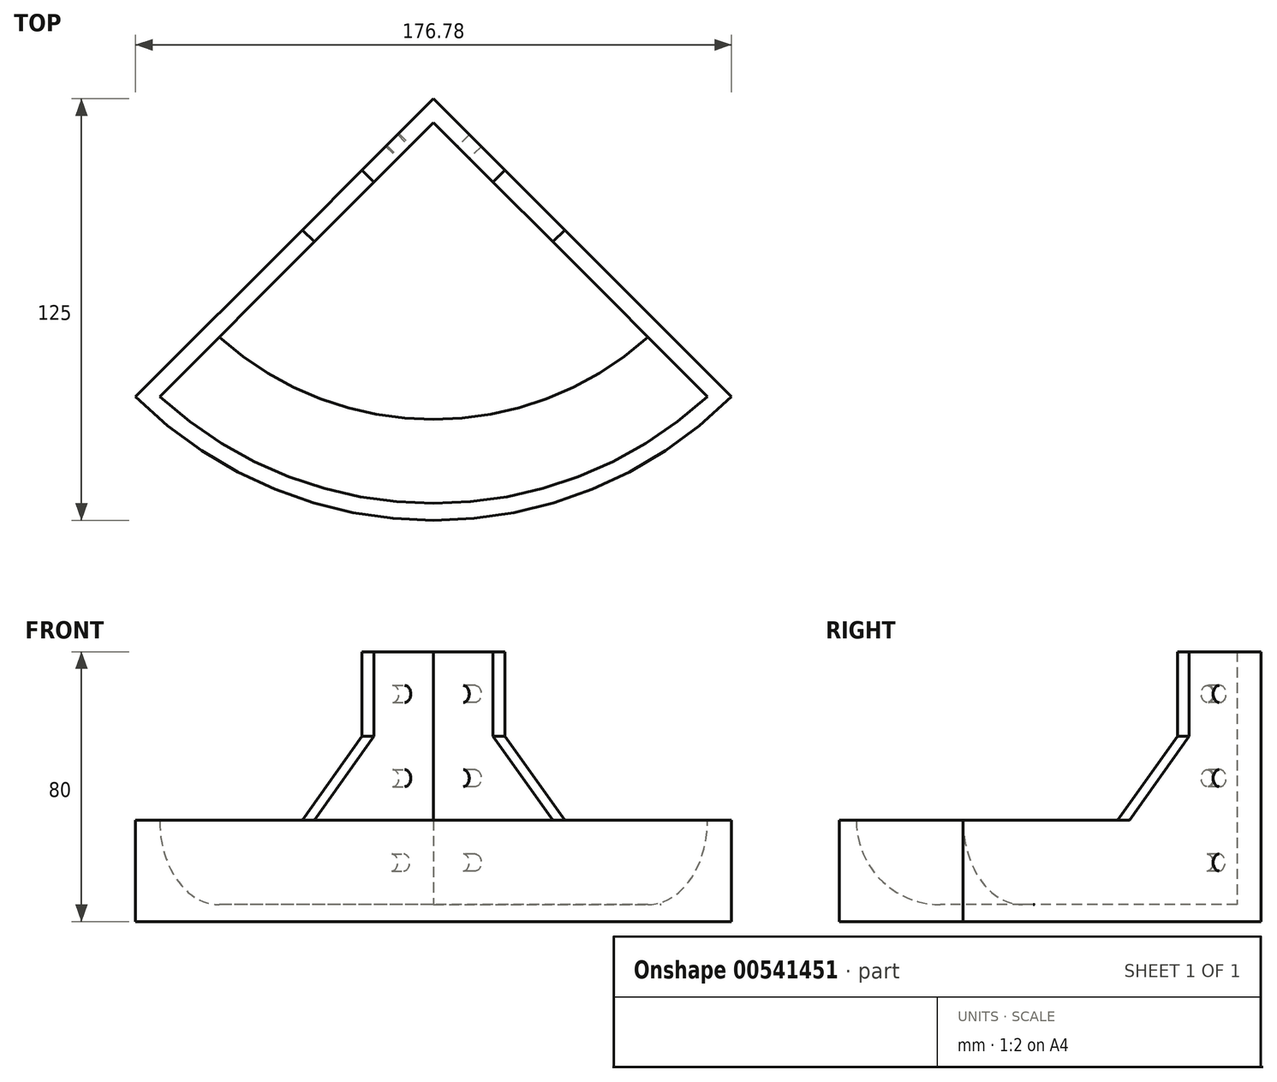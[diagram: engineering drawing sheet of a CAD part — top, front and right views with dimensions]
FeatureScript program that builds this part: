
annotation { "Feature Type Name" : "Feature", "Feature Type Description" : "" }
export const myFeature = defineFeature(function(context is Context, id is Id, definition is map)
    precondition{}
    {
        {
            var Q0;
            Q0=qCreatedBy(makeId("Top.planeOp"),FACE);
            var sketch = newSketch(context, id + "F0", { "sketchPlane" : qUnion([Q0])});
            skLineSegment(sketch, "E0", {"start": v(0, 0) * mm, "end": v(125, 0) * mm});
            skLineSegment(sketch, "E1", {"start": v(0, 0) * mm, "end": v(0, -125) * mm});
            skArc(sketch, "E2", {"start": v(0, -125) * mm, "mid": v(88.39, -88.39) * mm, "end": v(125, 0) * mm});
            skPoint(sketch, "E3", {"position": v(0, -120) * mm});
            skPoint(sketch, "E4", {"position": v(120, 0) * mm});
            skPoint(sketch, "E5", {"position": v(84.85, -84.85) * mm});
            skArc(sketch, "E6", {"start": v(0, -120) * mm, "mid": v(84.85, -84.85) * mm, "end": v(120, 0) * mm});
            skPoint(sketch, "E7", {"position": v(0, -5) * mm});
            skPoint(sketch, "E8", {"position": v(5, 0) * mm});
            skPoint(sketch, "E9", {"position": v(5, -5) * mm});
            skLineSegment(sketch, "E10", {"start": v(5, -5) * mm, "end": v(5, -119.9) * mm});
            skLineSegment(sketch, "E11", {"start": v(5, -5) * mm, "end": v(119.9, -5) * mm});
            skSolve(sketch);
        }
        {
            var Q0;
            {var subQ7=sQuery(id+"F0.wireOp",EDGE,"E10");Q0=makeQuery(id+"F0.imprint","IMPRINT",FACE,{"disambiguationData":[TD([[makeQuery(id+"F0.imprint","IMPRINT",EDGE,{"derivedFrom":subQ7}),-1.0]])]});}
            var Q1;
            {var subQ4=sQuery(id+"F0.wireOp",EDGE,"E2");Q1=makeQuery(id+"F0.imprint","IMPRINT",FACE,{"disambiguationData":[TD([[makeQuery(id+"F0.imprint","IMPRINT",EDGE,{"derivedFrom":subQ4}),1.0]])]});}
            var Q2;
            {var subQ0=sQuery(id+"F0.wireOp",EDGE,"E10");Q2=makeQuery(id+"F0.imprint","IMPRINT",FACE,{"disambiguationData":[TD([[makeQuery(id+"F0.imprint","IMPRINT",EDGE,{"derivedFrom":subQ0}),1.0]])]});}
            extrude(context, id + "F1", {"entities" : qUnion([Q0, Q1, Q2]), "depth" : 5 * mm, "offsetDistance" : 25 * mm});
        }
        {
            var Q0;
            Q0=makeQuery(id+"F1.opExtrude","CAP_FACE",FACE,{"disambiguationData":[OSD([sQuery(id+"F0.wireOp",EDGE,"E0"),sQuery(id+"F0.wireOp",EDGE,"E1"),sQuery(id+"F0.wireOp",EDGE,"E2")])],"isStart":false});
            var sketch = newSketch(context, id + "F2", { "sketchPlane" : qUnion([Q0])});
            skPoint(sketch, "E12", {"position": v(0, -120) * mm});
            skPoint(sketch, "E13", {"position": v(120, 0) * mm});
            skArc(sketch, "E14", {"start": v(0, -120) * mm, "mid": v(84.85, -84.85) * mm, "end": v(120, 0) * mm});
            skPoint(sketch, "E15", {"position": v(0, -5) * mm});
            skPoint(sketch, "E16", {"position": v(5, 0) * mm});
            skLineSegment(sketch, "E17", {"start": v(0, -5) * mm, "end": v(119.9, -5) * mm});
            skLineSegment(sketch, "E18", {"start": v(5, 0) * mm, "end": v(5, -119.9) * mm});
            skSolve(sketch);
        }
        {
            var Q0;
            {var subQ0=sQuery(id+"F2.wireOp",EDGE,"E17");var subQ1=makeQuery(id+"F1.opExtrude","CAP_EDGE",EDGE,{"disambiguationData":[OSD([sQuery(id+"F0.wireOp",EDGE,"E1")])],"isStart":false});var subQ2=makeQuery(id+"F2.imprint","INTERSECT",VERTEX,{"derivedFrom":[subQ1,subQ0]});Q0=makeQuery(id+"F2.imprint","IMPRINT",FACE,{"disambiguationData":[TD([[makeQuery(id+"F2.imprint","IMPRINT",EDGE,{"disambiguationData":[TD([[subQ2,-1.0]])],"derivedFrom":subQ0}),1.0]])]});}
            var Q1;
            {var subQ0=sQuery(id+"F2.wireOp",EDGE,"E14");var subQ1=makeQuery(id+"F1.opExtrude","CAP_EDGE",EDGE,{"disambiguationData":[OSD([sQuery(id+"F0.wireOp",EDGE,"E0")])],"isStart":false});var subQ2=makeQuery(id+"F2.imprint","INTERSECT",VERTEX,{"derivedFrom":[subQ1,subQ0]});Q1=makeQuery(id+"F2.imprint","IMPRINT",FACE,{"disambiguationData":[TD([[makeQuery(id+"F2.imprint","IMPRINT",EDGE,{"disambiguationData":[TD([[subQ2,1.0]])],"derivedFrom":subQ0}),1.0]])]});}
            var Q2;
            {var subQ0=sQuery(id+"F2.wireOp",EDGE,"E14");var subQ1=makeQuery(id+"F1.opExtrude","CAP_EDGE",EDGE,{"disambiguationData":[OSD([sQuery(id+"F0.wireOp",EDGE,"E1")])],"isStart":false});var subQ2=makeQuery(id+"F2.imprint","INTERSECT",VERTEX,{"derivedFrom":[subQ1,subQ0]});Q2=makeQuery(id+"F2.imprint","IMPRINT",FACE,{"disambiguationData":[TD([[makeQuery(id+"F2.imprint","IMPRINT",EDGE,{"disambiguationData":[TD([[subQ2,-1.0]])],"derivedFrom":subQ0}),1.0]])]});}
            var Q3;
            {var subQ0=makeQuery(id+"F1.opExtrude","CAP_EDGE",EDGE,{"disambiguationData":[OSD([sQuery(id+"F0.wireOp",EDGE,"E2")])],"isStart":false});Q3=makeQuery(id+"F2.imprint","IMPRINT",FACE,{"disambiguationData":[TD([[makeQuery(id+"F2.imprint","IMPRINT",EDGE,{"derivedFrom":subQ0}),1.0]])]});}
            extrude(context, id + "F3", {"entities" : qUnion([Q0, Q1, Q2, Q3]), "operationType" : NewBodyOperationType.ADD, "depth" : 25 * mm, "offsetDistance" : 25 * mm});
        }
        {
            var Q0;
            Q0=makeQuery(id+"F3.opExtrude","CAP_FACE",FACE,{"disambiguationData":[OSD([sQuery(id+"F0.wireOp",EDGE,"E0"),sQuery(id+"F0.wireOp",EDGE,"E1"),sQuery(id+"F0.wireOp",EDGE,"E2"),sQuery(id+"F2.wireOp",EDGE,"E14"),sQuery(id+"F2.wireOp",EDGE,"E17"),sQuery(id+"F2.wireOp",EDGE,"E18")])],"isStart":false});
            var sketch = newSketch(context, id + "F4", { "sketchPlane" : qUnion([Q0])});
            skPoint(sketch, "E19", {"position": v(5, -30) * mm});
            skLineSegment(sketch, "E20", {"start": v(5, -30) * mm, "end": v(0, -30) * mm});
            skPoint(sketch, "E21", {"position": v(30, -5) * mm});
            skLineSegment(sketch, "E22", {"start": v(30, -5) * mm, "end": v(30, 0) * mm});
            skSolve(sketch);
        }
        {
            var Q0;
            {var subQ3=sQuery(id+"F4.wireOp",EDGE,"E20");Q0=makeQuery(id+"F4.imprint","IMPRINT",FACE,{"disambiguationData":[TD([[makeQuery(id+"F4.imprint","IMPRINT",EDGE,{"derivedFrom":subQ3}),-1.0]])]});}
            extrude(context, id + "F5", {"entities" : qUnion([Q0]), "operationType" : NewBodyOperationType.ADD, "depth" : 50 * mm, "offsetDistance" : 25 * mm});
        }
        {
            var Q0;
            {var subQ0=sQuery(id+"F2.wireOp",EDGE,"E18");Q0=makeQuery(id+"F5.boolean.opBoolean","MERGE",FACE,{"derivedFrom":[makeQuery(id+"F3.opExtrude","SWEPT_FACE",FACE,{"disambiguationData":[OSD([subQ0])]}),makeQuery(id+"F5.opExtrude","SWEPT_FACE",FACE,{"disambiguationData":[OSD([subQ0])]})]});}
            var sketch = newSketch(context, id + "F6", { "sketchPlane" : qUnion([Q0])});
            skPoint(sketch, "E23", {"position": v(-17.03, 42.5) * mm});
            skPoint(sketch, "E24", {"position": v(-17.03, 67.5) * mm});
            skLineSegment(sketch, "E25", {"start": v(-30, 30) * mm, "end": v(-17.5, 30) * mm});
            skLineSegment(sketch, "E26", {"start": v(-17.5, 30) * mm, "end": v(-17.5, 17.5) * mm});
            skSolve(sketch);
        }
        {
            var Q0;
            Q0=sQuery(id+"F6.wireOp",VERTEX,"E26.end");
            var Q1;
            Q1=sQuery(id+"F6.wireOp",VERTEX,"E23");
            var Q2;
            Q2=sQuery(id+"F6.wireOp",VERTEX,"E24");
            var Q3;
            Q3=makeQuery(id+"F1.opExtrude","SWEPT_BODY",BODY,{"disambiguationData":[OSD([sQuery(id+"F0.wireOp",EDGE,"E0"),sQuery(id+"F0.wireOp",EDGE,"E1"),sQuery(id+"F0.wireOp",EDGE,"E2")])]});
            hole(context, id + "F7", {"style" : HoleStyle.SIMPLE, "endStyle" : HoleEndStyle.BLIND, "holeDiameter" : 5 * mm, "holeDepth" : 10 * mm, "isTappedThrough" : true, "tappedDepth" : 1 * mm, "tapClearance" : 3, "locations" : qUnion([Q0, Q1, Q2]), "scope" : qUnion([Q3])});
        }
        {
            var Q0;
            {var subQ0=sQuery(id+"F2.wireOp",EDGE,"E17");Q0=makeQuery(id+"F5.boolean.opBoolean","MERGE",FACE,{"derivedFrom":[makeQuery(id+"F3.opExtrude","SWEPT_FACE",FACE,{"disambiguationData":[OSD([subQ0])]}),makeQuery(id+"F5.opExtrude","SWEPT_FACE",FACE,{"disambiguationData":[OSD([subQ0])]})]});}
            var sketch = newSketch(context, id + "F8", { "sketchPlane" : qUnion([Q0])});
            skLineSegment(sketch, "E27", {"start": v(30, 30) * mm, "end": v(17.5, 30) * mm});
            skLineSegment(sketch, "E28", {"start": v(17.5, 30) * mm, "end": v(17.5, 17.5) * mm});
            skPoint(sketch, "E29", {"position": v(17.5, 42.5) * mm});
            skPoint(sketch, "E29.positionSnap0", {"position": v(17.5, 23.75) * mm});
            skPoint(sketch, "E30", {"position": v(17.5, 67.5) * mm});
            skSolve(sketch);
        }
        {
            var Q0;
            Q0=sQuery(id+"F8.wireOp",VERTEX,"E28.end");
            var Q1;
            Q1=sQuery(id+"F8.wireOp",VERTEX,"E29");
            var Q2;
            Q2=sQuery(id+"F8.wireOp",VERTEX,"E30");
            var Q3;
            Q3=makeQuery(id+"F1.opExtrude","SWEPT_BODY",BODY,{"disambiguationData":[OSD([sQuery(id+"F0.wireOp",EDGE,"E0"),sQuery(id+"F0.wireOp",EDGE,"E1"),sQuery(id+"F0.wireOp",EDGE,"E2")])]});
            hole(context, id + "F9", {"style" : HoleStyle.SIMPLE, "endStyle" : HoleEndStyle.BLIND, "holeDiameter" : 5 * mm, "holeDepth" : 10 * mm, "isTappedThrough" : true, "tappedDepth" : 1 * mm, "tapClearance" : 3, "locations" : qUnion([Q0, Q1, Q2]), "scope" : qUnion([Q3])});
        }
        {
            var Q0;
            Q0=makeQuery(id+"F1.opExtrude","SWEPT_BODY",BODY,{"disambiguationData":[OSD([sQuery(id+"F0.wireOp",EDGE,"E0"),sQuery(id+"F0.wireOp",EDGE,"E1"),sQuery(id+"F0.wireOp",EDGE,"E2")])]});
            var Q1;
            {var subQ0=sQuery(id+"F0.wireOp",EDGE,"E2");Q1=makeQuery(id+"F3.boolean.opBoolean","MERGE",FACE,{"derivedFrom":[makeQuery(id+"F1.opExtrude","SWEPT_FACE",FACE,{"disambiguationData":[OSD([subQ0])]}),makeQuery(id+"F3.opExtrude","SWEPT_FACE",FACE,{"disambiguationData":[OSD([subQ0])]})]});}
            transform(context, id + "F10", {"entities" : qUnion([Q0]), "transformType" : TransformType.ROTATION, "transformAxis" : qUnion([Q1]), "angle" : 45 * degree, "makeCopy" : false});
        }
        {
            var Q0;
            {var subQ0=sQuery(id+"F2.wireOp",EDGE,"E18");Q0=makeQuery(id+"F5.boolean.opBoolean","MERGE",FACE,{"derivedFrom":[makeQuery(id+"F3.opExtrude","SWEPT_FACE",FACE,{"disambiguationData":[OSD([subQ0])]}),makeQuery(id+"F5.opExtrude","SWEPT_FACE",FACE,{"disambiguationData":[OSD([subQ0])]})]});}
            var sketch = newSketch(context, id + "F11", { "sketchPlane" : qUnion([Q0])});
            skPoint(sketch, "E31", {"position": v(-30, 55) * mm});
            skPoint(sketch, "E32", {"position": v(-55, 30) * mm});
            skLineSegment(sketch, "E33", {"start": v(-55, 30) * mm, "end": v(-30, 55) * mm});
            skSolve(sketch);
        }
        {
            var Q0;
            {var subQ0=sQuery(id+"F11.wireOp",EDGE,"E33");Q0=makeQuery(id+"F11.imprint","IMPRINT",FACE,{"disambiguationData":[TD([[makeQuery(id+"F11.imprint","IMPRINT",EDGE,{"derivedFrom":subQ0}),-1.0]])]});}
            var Q1;
            {var subQ0=sQuery(id+"F0.wireOp",EDGE,"E1");Q1=makeQuery(id+"F5.boolean.opBoolean","MERGE",FACE,{"derivedFrom":[makeQuery(id+"F3.boolean.opBoolean","MERGE",FACE,{"derivedFrom":[makeQuery(id+"F1.opExtrude","SWEPT_FACE",FACE,{"disambiguationData":[OSD([subQ0])]}),makeQuery(id+"F3.opExtrude","SWEPT_FACE",FACE,{"disambiguationData":[OSD([subQ0])]})]}),makeQuery(id+"F5.opExtrude","SWEPT_FACE",FACE,{"disambiguationData":[OSD([subQ0])]})]});}
            extrude(context, id + "F12", {"entities" : qUnion([Q0]), "operationType" : NewBodyOperationType.ADD, "endBound" : BoundingType.UP_TO_SURFACE, "oppositeDirection" : true, "depth" : 25 * mm, "endBoundEntityFace" : qUnion([Q1]), "offsetDistance" : 25 * mm});
        }
        {
            var Q0;
            {var subQ0=sQuery(id+"F2.wireOp",EDGE,"E17");Q0=makeQuery(id+"F5.boolean.opBoolean","MERGE",FACE,{"derivedFrom":[makeQuery(id+"F3.opExtrude","SWEPT_FACE",FACE,{"disambiguationData":[OSD([subQ0])]}),makeQuery(id+"F5.opExtrude","SWEPT_FACE",FACE,{"disambiguationData":[OSD([subQ0])]})]});}
            var sketch = newSketch(context, id + "F13", { "sketchPlane" : qUnion([Q0])});
            skPoint(sketch, "E34", {"position": v(30, 55) * mm});
            skPoint(sketch, "E35", {"position": v(55, 30) * mm});
            skLineSegment(sketch, "E36", {"start": v(30, 55) * mm, "end": v(55, 30) * mm});
            skSolve(sketch);
        }
        {
            var Q0;
            {var subQ0=sQuery(id+"F13.wireOp",EDGE,"E36");Q0=makeQuery(id+"F13.imprint","IMPRINT",FACE,{"disambiguationData":[TD([[makeQuery(id+"F13.imprint","IMPRINT",EDGE,{"derivedFrom":subQ0}),-1.0]])]});}
            var Q1;
            {var subQ0=sQuery(id+"F0.wireOp",EDGE,"E0");Q1=makeQuery(id+"F5.boolean.opBoolean","MERGE",FACE,{"derivedFrom":[makeQuery(id+"F3.boolean.opBoolean","MERGE",FACE,{"derivedFrom":[makeQuery(id+"F1.opExtrude","SWEPT_FACE",FACE,{"disambiguationData":[OSD([subQ0])]}),makeQuery(id+"F3.opExtrude","SWEPT_FACE",FACE,{"disambiguationData":[OSD([subQ0])]})]}),makeQuery(id+"F5.opExtrude","SWEPT_FACE",FACE,{"disambiguationData":[OSD([subQ0])]})]});}
            extrude(context, id + "F14", {"entities" : qUnion([Q0]), "operationType" : NewBodyOperationType.ADD, "endBound" : BoundingType.UP_TO_SURFACE, "oppositeDirection" : true, "depth" : 25 * mm, "endBoundEntityFace" : qUnion([Q1]), "offsetDistance" : 25 * mm});
        }
        {
            var Q0;
            {var subQ0=sQuery(id+"F2.wireOp",EDGE,"E18");Q0=makeQuery(id+"F12.boolean.opBoolean","MERGE",FACE,{"derivedFrom":[makeQuery(id+"F5.boolean.opBoolean","MERGE",FACE,{"derivedFrom":[makeQuery(id+"F3.opExtrude","SWEPT_FACE",FACE,{"disambiguationData":[OSD([subQ0])]}),makeQuery(id+"F5.opExtrude","SWEPT_FACE",FACE,{"disambiguationData":[OSD([subQ0])]})]}),makeQuery(id+"F12.opExtrude","CAP_FACE",FACE,{"disambiguationData":[OSD([subQ0,sQuery(id+"F4.wireOp",EDGE,"E20"),sQuery(id+"F11.wireOp",EDGE,"E33")])],"isStart":true})]});}
            var sketch = newSketch(context, id + "F15", { "sketchPlane" : qUnion([Q0])});
            skPoint(sketch, "E37", {"position": v(-94.9, 30) * mm});
            skArc(sketch, "E38", {"start": v(-119.9, 30) * mm, "mid": v(-112.57, 12.32) * mm, "end": v(-94.9, 5) * mm});
            skSolve(sketch);
        }
        {
            var Q0;
            {var subQ0=sQuery(id+"F15.wireOp",EDGE,"E38");Q0=makeQuery(id+"F15.imprint","IMPRINT",FACE,{"disambiguationData":[TD([[makeQuery(id+"F15.imprint","IMPRINT",EDGE,{"derivedFrom":subQ0}),-1.0]])]});}
            var Q1;
            Q1=makeQuery(id+"F3.opExtrude","SWEPT_FACE",FACE,{"disambiguationData":[OSD([sQuery(id+"F2.wireOp",EDGE,"E14")])]});
            revolve(context, id + "F16", {"operationType" : NewBodyOperationType.ADD, "entities" : qUnion([Q0]), "axis" : qUnion([Q1]), "revolveType" : RevolveType.ONE_DIRECTION, "angle" : 87 * degree});
        }
    });
